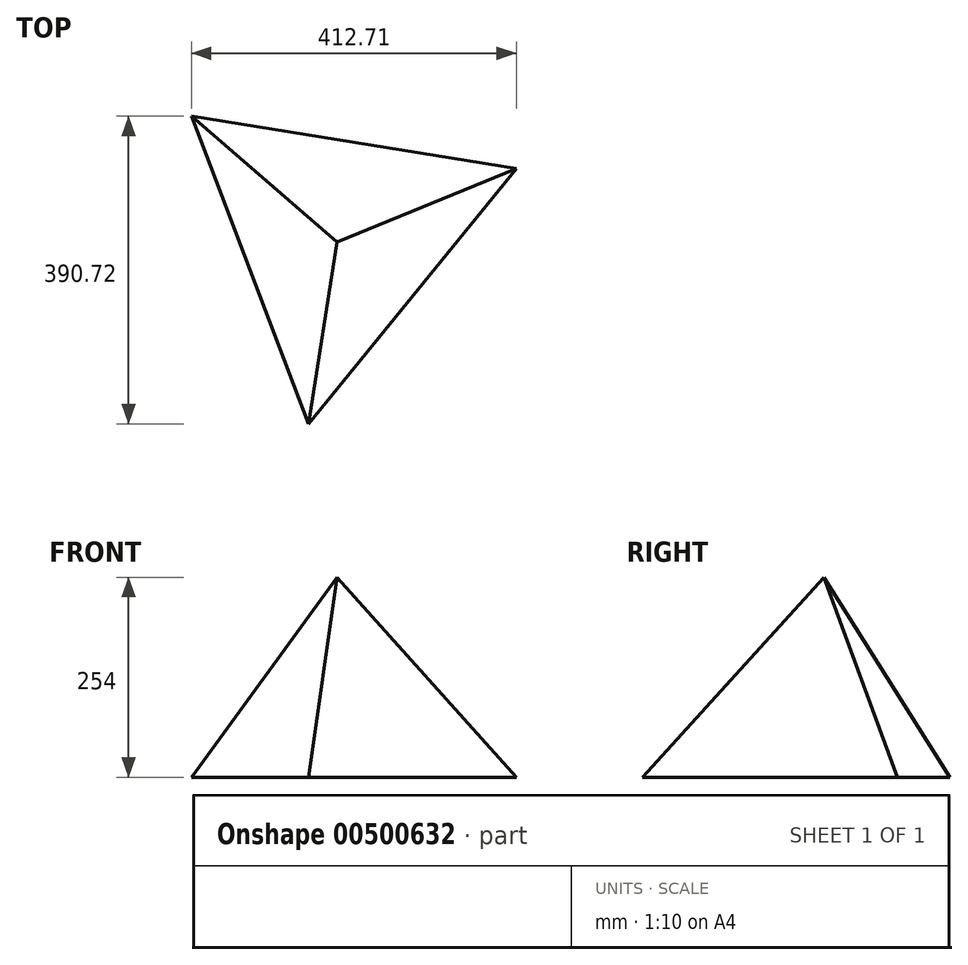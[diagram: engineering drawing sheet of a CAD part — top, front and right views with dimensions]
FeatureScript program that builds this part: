
annotation { "Feature Type Name" : "Feature", "Feature Type Description" : "" }
export const myFeature = defineFeature(function(context is Context, id is Id, definition is map)
    precondition{}
    {
        {
            var Q0;
            Q0=qCreatedBy(makeId("Top.planeOp"),FACE);
            var sketch = newSketch(context, id + "F0", { "sketchPlane" : qUnion([Q0])});
            skCircle(sketch, "E0.cCircle", {"center": v(0, 0) * mm, "radius": 120.68 * mm, "construction": true});
            skLineSegment(sketch, "E0.0", {"start": v(225.58, 85.84) * mm, "end": v(-38.45, -238.28) * mm});
            skLineSegment(sketch, "E0.1", {"start": v(-38.45, -238.28) * mm, "end": v(-187.13, 152.44) * mm});
            skLineSegment(sketch, "E0.2", {"start": v(-187.13, 152.44) * mm, "end": v(225.58, 85.84) * mm});
            skPoint(sketch, "E0.0.midPoint", {"position": v(93.56, -76.22) * mm});
            skSolve(sketch);
        }
        {
            var Q0;
            Q0=qCreatedBy(makeId("Top.planeOp"),FACE);
            cPlane(context, id + "F1", {"entities" : qUnion([Q0]), "cplaneType" : CPlaneType.OFFSET, "offset" : 254 * mm, "width" : 152.4 * mm, "height" : 152.4 * mm});
        }
        {
            var Q0;
            Q0=qCreatedBy(id+"F1.planeOp",FACE);
            var sketch = newSketch(context, id + "F2", { "sketchPlane" : qUnion([Q0])});
            skPoint(sketch, "E1", {"position": v(-2.07, -7.38) * mm});
            skSolve(sketch);
        }
        {
            var Q0;
            Q0=makeQuery(id+"F0.imprint","IMPRINT",FACE,{"disambiguationData":[TD([[makeQuery(id+"F0.imprint","IMPRINT",EDGE,{"derivedFrom":sQuery(id+"F0.wireOp",EDGE,"E0.0")}),-1.0]])]});
            var Q1;
            Q1=sQuery(id+"F2.wireOp",VERTEX,"E1");
            loft(context, id + "F3", {"sheetProfilesArray" : [{ "sheetProfileEntities" : qUnion([Q0]) }, { "sheetProfileEntities" : qUnion([Q1]) }]});
        }
    });
